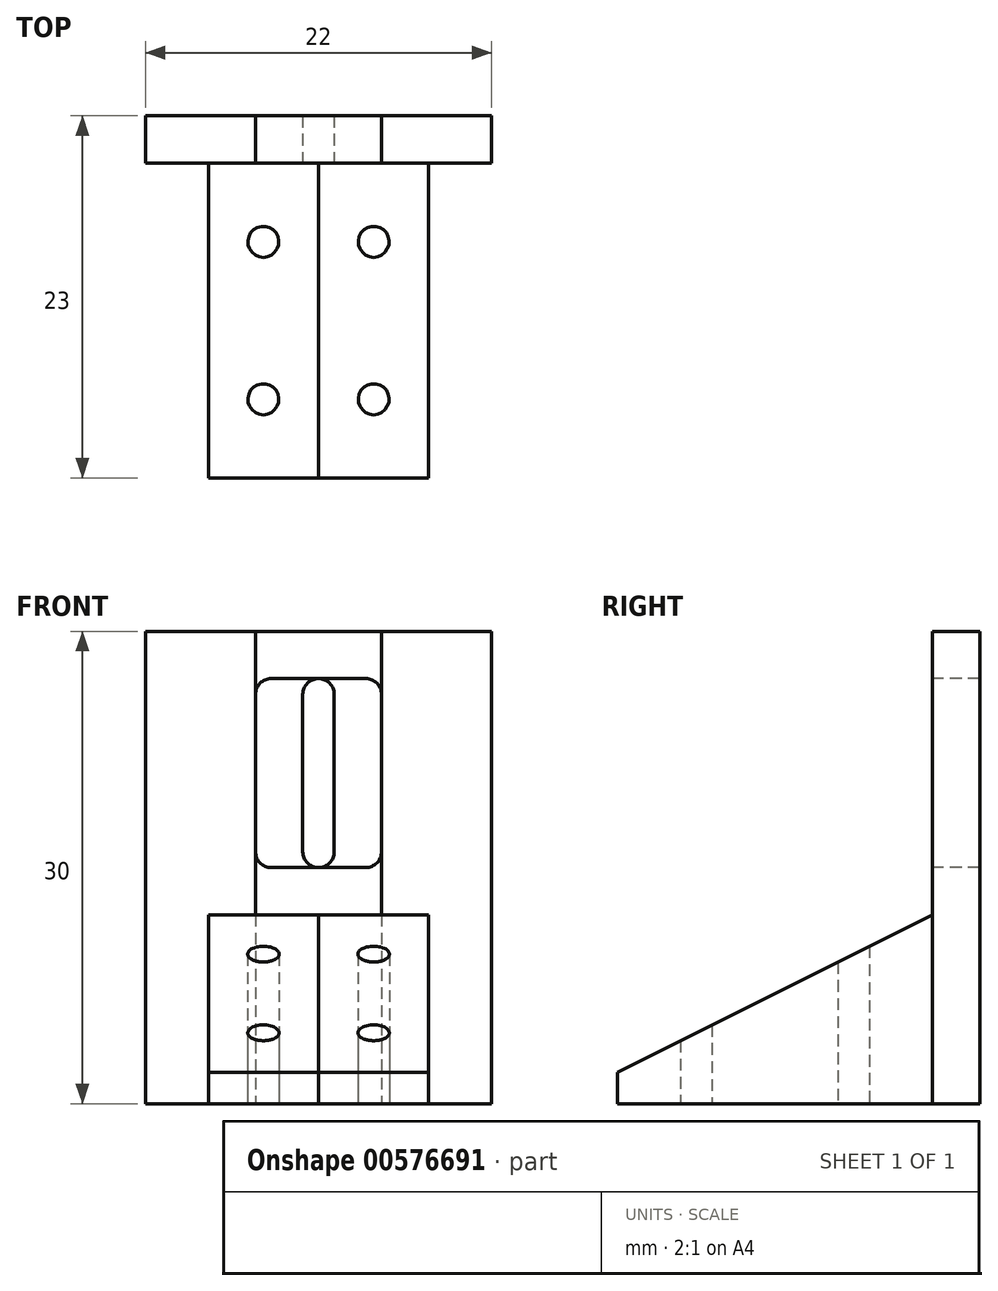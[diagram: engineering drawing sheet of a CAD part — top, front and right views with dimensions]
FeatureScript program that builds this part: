
annotation { "Feature Type Name" : "Feature", "Feature Type Description" : "" }
export const myFeature = defineFeature(function(context is Context, id is Id, definition is map)
    precondition{}
    {
        {
            var Q0;
            Q0=qCreatedBy(makeId("Top.planeOp"),FACE);
            var sketch = newSketch(context, id + "F0", { "sketchPlane" : qUnion([Q0])});
            skLineSegment(sketch, "E0.bottom", {"start": v(0, 0) * mm, "end": v(7, 0) * mm});
            skLineSegment(sketch, "E0.top", {"start": v(0, 20) * mm, "end": v(7, 20) * mm});
            skLineSegment(sketch, "E0.left", {"start": v(0, 0) * mm, "end": v(0, 20) * mm});
            skLineSegment(sketch, "E0.right", {"start": v(7, 0) * mm, "end": v(7, 20) * mm});
            skCircle(sketch, "E1", {"center": v(3.5, 15) * mm, "radius": 1 * mm});
            skCircle(sketch, "E2.MirrorC", {"center": v(3.5, 5) * mm, "radius": 1 * mm});
            skSolve(sketch);
        }
        {
            var Q0;
            Q0 = qSketchRegion(id + "F0", true);
            extrude(context, id + "F1", {"entities" : qUnion([Q0]), "depth" : 12 * mm, "offsetDistance" : 25.4 * mm});
        }
        {
            var Q0;
            Q0=qCreatedBy(makeId("Top.planeOp"),FACE);
            var sketch = newSketch(context, id + "F2", { "sketchPlane" : qUnion([Q0])});
            skLineSegment(sketch, "E3.bottom", {"start": v(7, 20) * mm, "end": v(-4, 20) * mm});
            skLineSegment(sketch, "E3.top", {"start": v(7, 23) * mm, "end": v(-4, 23) * mm});
            skLineSegment(sketch, "E3.right", {"start": v(-4, 20) * mm, "end": v(-4, 23) * mm});
            skLineSegment(sketch, "E4", {"start": v(7, 23) * mm, "end": v(11, 23) * mm});
            skLineSegment(sketch, "E5", {"start": v(11, 23) * mm, "end": v(11, 20) * mm});
            skLineSegment(sketch, "E6", {"start": v(7, 20) * mm, "end": v(11, 20) * mm});
            skSolve(sketch);
        }
        {
            var Q0;
            Q0 = qSketchRegion(id + "F2", true);
            extrude(context, id + "F3", {"entities" : qUnion([Q0]), "operationType" : NewBodyOperationType.ADD, "depth" : 30 * mm, "offsetDistance" : 25.4 * mm});
        }
        {
            var Q0;
            Q0=qCreatedBy(makeId("Right.planeOp"),FACE);
            var sketch = newSketch(context, id + "F4", { "sketchPlane" : qUnion([Q0])});
            skLineSegment(sketch, "E7", {"start": v(20, 12) * mm, "end": v(0, 2) * mm});
            skLineSegment(sketch, "E8", {"start": v(0, 2) * mm, "end": v(0, 12) * mm});
            skLineSegment(sketch, "E9", {"start": v(20, 12) * mm, "end": v(0, 12) * mm});
            skPoint(sketch, "E10.start.orphan", {"position": v(0, 0) * mm});
            skSolve(sketch);
        }
        {
            var Q0;
            Q0 = qSketchRegion(id + "F4", true);
            extrude(context, id + "F5", {"entities" : qUnion([Q0]), "operationType" : NewBodyOperationType.REMOVE, "depth" : 10 * mm, "offsetDistance" : 25.4 * mm});
        }
        {
            var Q0;
            Q0=qCreatedBy(makeId("Front.planeOp"),FACE);
            var sketch = newSketch(context, id + "F6", { "sketchPlane" : qUnion([Q0])});
            skLineSegment(sketch, "E11.bottom", {"start": v(3, 15) * mm, "end": v(0, 15) * mm});
            skLineSegment(sketch, "E11.top", {"start": v(3, 27) * mm, "end": v(0, 27) * mm});
            skLineSegment(sketch, "E11.left", {"start": v(4, 16) * mm, "end": v(4, 26) * mm});
            skLineSegment(sketch, "E11.right", {"start": v(-1, 16) * mm, "end": v(-1, 26) * mm});
            skPoint(sketch, "E12.visualSharp", {"position": v(4, 15) * mm});
            skArc(sketch, "E12.filletArc", {"start": v(3, 15) * mm, "mid": v(3.7, 15.3) * mm, "end": v(4, 16) * mm});
            skPoint(sketch, "E13.visualSharp", {"position": v(-1, 15) * mm});
            skArc(sketch, "E13.filletArc", {"start": v(-1, 16) * mm, "mid": v(-0.7, 15.3) * mm, "end": v(0, 15) * mm});
            skPoint(sketch, "E14.visualSharp", {"position": v(-1, 27) * mm});
            skArc(sketch, "E14.filletArc", {"start": v(0, 27) * mm, "mid": v(-0.7, 26.7) * mm, "end": v(-1, 26) * mm});
            skPoint(sketch, "E15.visualSharp", {"position": v(4, 27) * mm});
            skArc(sketch, "E15.filletArc", {"start": v(4, 26) * mm, "mid": v(3.7, 26.7) * mm, "end": v(3, 27) * mm});
            skSolve(sketch);
        }
        {
            var Q0;
            Q0 = qSketchRegion(id + "F6", true);
            extrude(context, id + "F7", {"entities" : qUnion([Q0]), "operationType" : NewBodyOperationType.REMOVE, "oppositeDirection" : true, "depth" : 25.4 * mm, "offsetDistance" : 25.4 * mm});
        }
        {
            var Q0;
            Q0=makeQuery(id+"F1.opExtrude","SWEPT_BODY",BODY,{"disambiguationData":[OSD([sQuery(id+"F0.wireOp",EDGE,"E0.bottom"),sQuery(id+"F0.wireOp",EDGE,"E0.top"),sQuery(id+"F0.wireOp",EDGE,"E0.left"),sQuery(id+"F0.wireOp",EDGE,"E0.right"),sQuery(id+"F0.wireOp",EDGE,"E1"),sQuery(id+"F0.wireOp",EDGE,"E2.MirrorC")])]});
            var Q1;
            Q1=qCreatedBy(makeId("Right.planeOp"),FACE);
            mirror(context, id + "F8", {"entities" : qUnion([Q0]), "mirrorPlane" : qUnion([Q1])});
        }
    });
